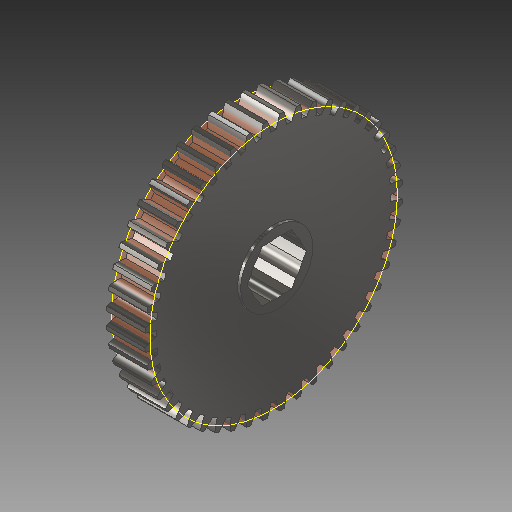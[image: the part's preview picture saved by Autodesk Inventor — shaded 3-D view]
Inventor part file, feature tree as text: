
AUTODESK INVENTOR PART (.ipt)
format: ipt  version: 2018 (Build 220112000, 112)  size: 352,768 bytes
history: native  units: in
note: dims shown in document units (in); Inventor stores cm internally (conversion verified against a paired STEP export)
features: other x3, sketch x1
ambient origin geometry x8: Origin, YZ Plane, XZ Plane, XY Plane, X Axis, Y Axis, Z Axis, Center Point
bodies: Solid1 (feature_tree)
feature tree (4):
  sketch  "Sketch1"  dims[d0=2.4in d1=1.0in d2=0.0in]
  other  "Srf1"
  other  "Cut-Extrude3"
  other  "pitch circle"
